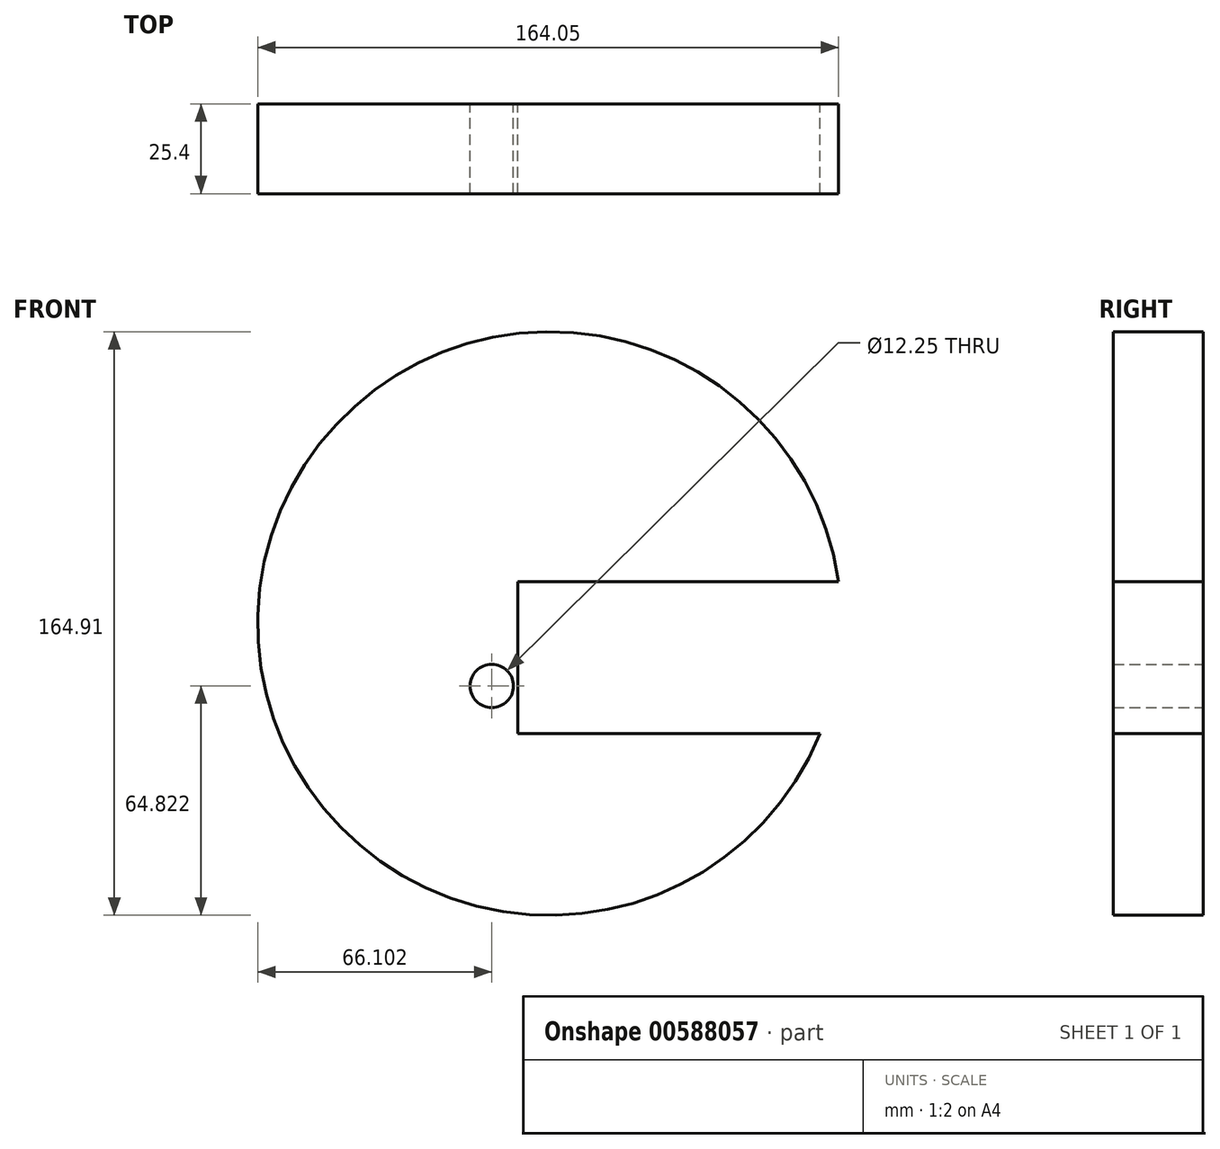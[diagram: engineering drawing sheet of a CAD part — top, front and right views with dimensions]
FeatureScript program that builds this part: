
annotation { "Feature Type Name" : "Feature", "Feature Type Description" : "" }
export const myFeature = defineFeature(function(context is Context, id is Id, definition is map)
    precondition{}
    {
        {
            var Q0;
            Q0=qCreatedBy(makeId("Front.planeOp"),FACE);
            var sketch = newSketch(context, id + "F0", { "sketchPlane" : qUnion([Q0])});
            skLineSegment(sketch, "E0.bottom", {"start": v(-57.4, 25.65) * mm, "end": v(63.82, 25.65) * mm});
            skLineSegment(sketch, "E0.top", {"start": v(-57.4, -17.32) * mm, "end": v(63.82, -17.32) * mm});
            skLineSegment(sketch, "E0.left", {"start": v(-57.4, 25.65) * mm, "end": v(-57.4, -17.32) * mm});
            skLineSegment(sketch, "E0.right", {"start": v(63.82, 25.65) * mm, "end": v(63.82, -17.32) * mm});
            skCircle(sketch, "E1", {"center": v(-48.42, 19.24) * mm, "radius": 3.03 * mm});
            skCircle(sketch, "E2", {"center": v(-64.78, -3.85) * mm, "radius": 6.13 * mm});
            skCircle(sketch, "E3", {"center": v(-48.42, 19.24) * mm, "radius": 2.59 * mm});
            skCircle(sketch, "E4", {"center": v(-48.42, 13.79) * mm, "radius": 2.87 * mm});
            skCircle(sketch, "E5", {"center": v(-48.42, 13.79) * mm, "radius": 82.45 * mm});
            skSolve(sketch);
        }
        {
            var Q0;
            {var subQ0=sQuery(id+"F0.wireOp",EDGE,"E0.left");Q0=makeQuery(id+"F0.imprint","IMPRINT",FACE,{"disambiguationData":[TD([[makeQuery(id+"F0.imprint","IMPRINT",EDGE,{"derivedFrom":subQ0}),-1.0]])]});}
            extrude(context, id + "F1", {"entities" : qUnion([Q0]), "depth" : 25.4 * mm, "offsetDistance" : 25.4 * mm});
        }
    });
